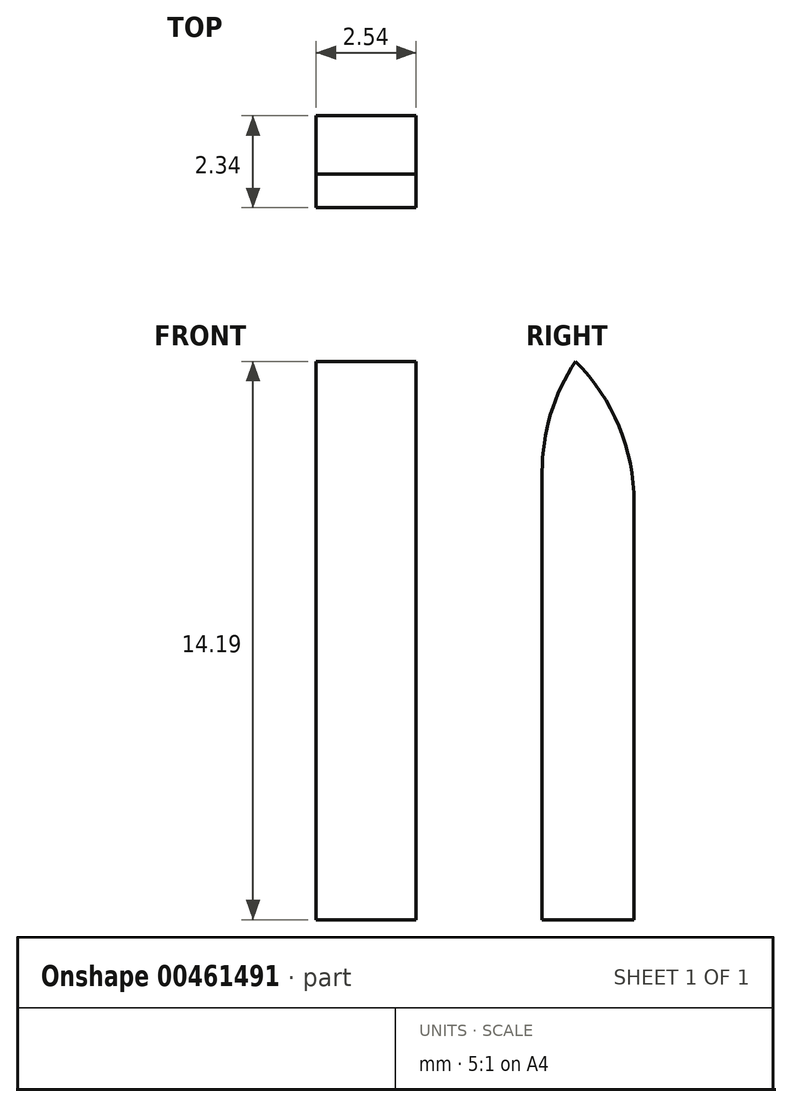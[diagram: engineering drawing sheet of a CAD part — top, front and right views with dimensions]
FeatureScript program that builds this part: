
annotation { "Feature Type Name" : "Feature", "Feature Type Description" : "" }
export const myFeature = defineFeature(function(context is Context, id is Id, definition is map)
    precondition{}
    {
        {
            var Q0;
            Q0=qCreatedBy(makeId("Top.planeOp"),FACE);
            var sketch = newSketch(context, id + "F0", { "sketchPlane" : qUnion([Q0])});
            skLineSegment(sketch, "E0.bottom", {"start": v(11.9, 0.7) * mm, "end": v(14.45, 0.7) * mm});
            skLineSegment(sketch, "E0.top", {"start": v(11.9, -1.64) * mm, "end": v(14.45, -1.64) * mm});
            skLineSegment(sketch, "E0.left", {"start": v(11.9, 0.7) * mm, "end": v(11.9, -1.64) * mm});
            skLineSegment(sketch, "E0.right", {"start": v(14.45, 0.7) * mm, "end": v(14.45, -1.64) * mm});
            skSolve(sketch);
        }
        {
            var Q0;
            Q0=makeQuery(id+"F0.imprint","IMPRINT",FACE,{"disambiguationData":[TD([[makeQuery(id+"F0.imprint","IMPRINT",EDGE,{"derivedFrom":sQuery(id+"F0.wireOp",EDGE,"E0.bottom")}),-1.0]])]});
            extrude(context, id + "F1", {"entities" : qUnion([Q0]), "depth" : 25.4 * mm});
        }
        {
            var Q0;
            Q0=makeQuery(id+"F1.opExtrude","CAP_EDGE",EDGE,{"disambiguationData":[OSD([sQuery(id+"F0.wireOp",EDGE,"E0.bottom")])],"isStart":false});
            chamfer(context, id + "F2", {"entities" : qUnion([Q0]), "width" : 12.7 * mm, "tangentPropagation" : true});
        }
        {
            var Q0;
            {var subQ0=sQuery(id+"F0.wireOp",EDGE,"E0.bottom");Q0=makeQuery(id+"F2.opChamfer","BLEND_EDGE",EDGE,{"blendedFrom":[makeQuery(id+"F1.opExtrude","CAP_EDGE",EDGE,{"disambiguationData":[OSD([subQ0])],"isStart":false}),makeQuery(id+"F1.opExtrude","SWEPT_FACE",FACE,{"disambiguationData":[OSD([subQ0])]})],"blendedInto":[makeQuery(id+"F1.opExtrude","SWEPT_FACE",FACE,{"disambiguationData":[OSD([subQ0])]})]});}
            fillet(context, id + "F3", {"entities" : qUnion([Q0]), "radius" : 5.08 * mm, "tangentPropagation" : true, "allowEdgeOverflow" : false});
        }
        {
            var Q0;
            Q0=makeQuery(id+"F2.opChamfer","BLEND_EDGE",EDGE,{"blendedFrom":[makeQuery(id+"F1.opExtrude","CAP_EDGE",EDGE,{"disambiguationData":[OSD([sQuery(id+"F0.wireOp",EDGE,"E0.bottom")])],"isStart":false}),makeQuery(id+"F1.opExtrude","SWEPT_FACE",FACE,{"disambiguationData":[OSD([sQuery(id+"F0.wireOp",EDGE,"E0.top")])]})],"blendedInto":[makeQuery(id+"F1.opExtrude","SWEPT_FACE",FACE,{"disambiguationData":[OSD([sQuery(id+"F0.wireOp",EDGE,"E0.top")])]})]});
            fillet(context, id + "F4", {"entities" : qUnion([Q0]), "radius" : 5.08 * mm, "tangentPropagation" : true, "allowEdgeOverflow" : false});
        }
    });
